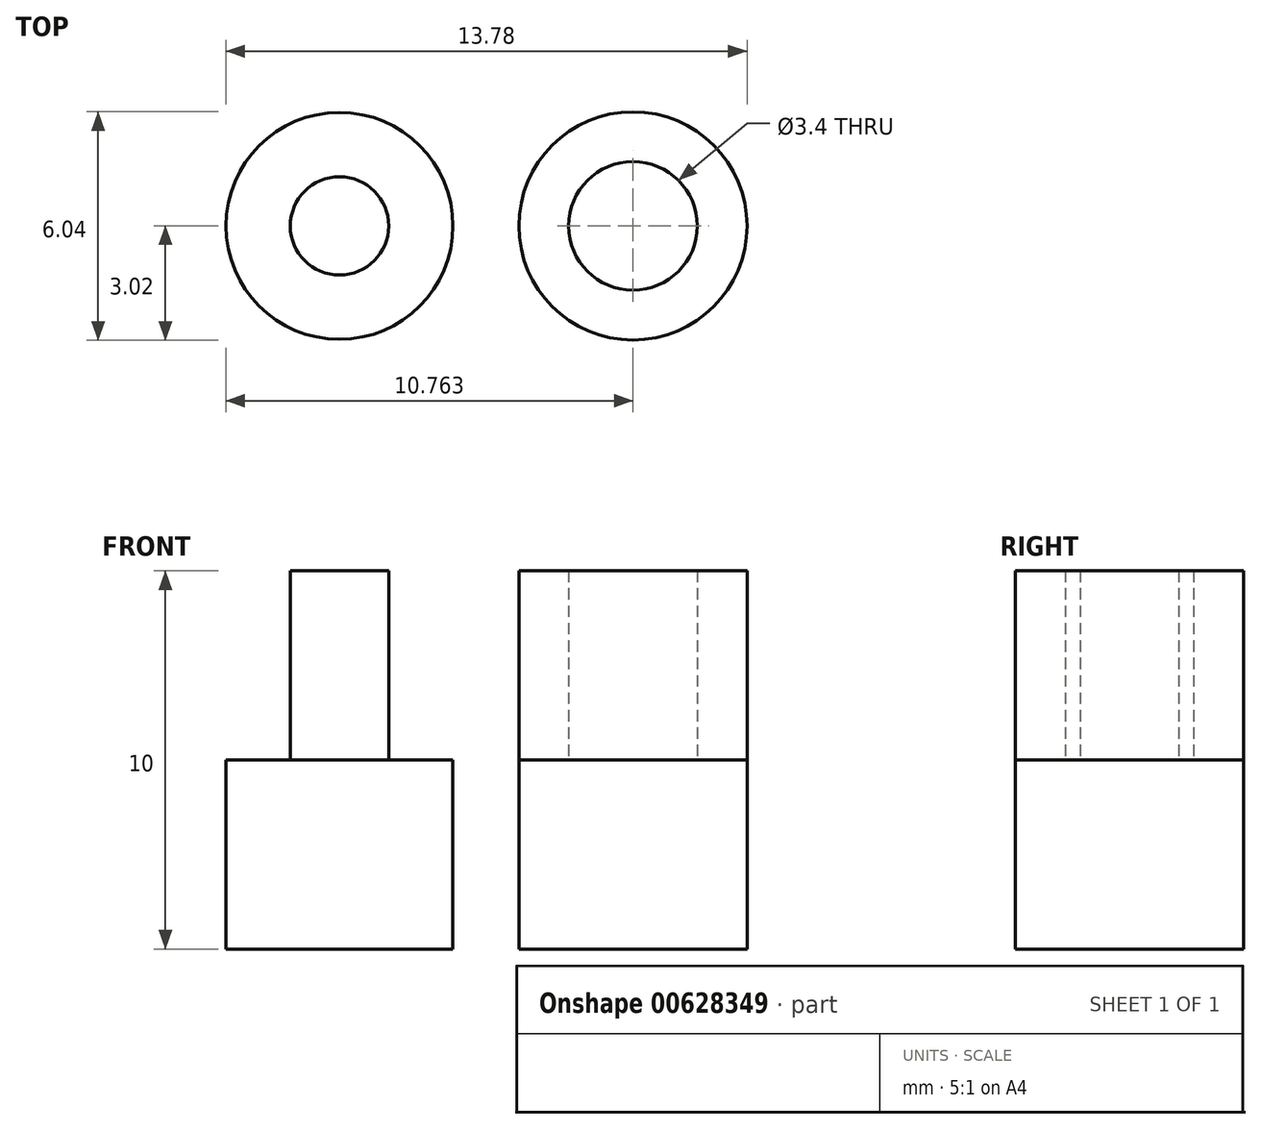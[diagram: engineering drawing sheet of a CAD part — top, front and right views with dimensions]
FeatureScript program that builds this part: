
annotation { "Feature Type Name" : "Feature", "Feature Type Description" : "" }
export const myFeature = defineFeature(function(context is Context, id is Id, definition is map)
    precondition{}
    {
        {
            var Q0;
            Q0=qCreatedBy(makeId("Top.planeOp"),FACE);
            var sketch = newSketch(context, id + "F0", { "sketchPlane" : qUnion([Q0])});
            skCircle(sketch, "E0", {"center": v(-33.58, 0) * mm, "radius": 3 * mm});
            skCircle(sketch, "E1", {"center": v(-25.82, 0) * mm, "radius": 3.02 * mm});
            skCircle(sketch, "E2", {"center": v(-33.58, 0) * mm, "radius": 1.3 * mm});
            skCircle(sketch, "E3", {"center": v(-25.82, 0) * mm, "radius": 1.7 * mm});
            skSolve(sketch);
        }
        {
            var Q0;
            Q0=makeQuery(id+"F0.imprint","IMPRINT",FACE,{"disambiguationData":[TD([[makeQuery(id+"F0.imprint","IMPRINT",EDGE,{"derivedFrom":sQuery(id+"F0.wireOp",EDGE,"E2")}),1.0]])]});
            var Q1;
            Q1=makeQuery(id+"F0.imprint","IMPRINT",FACE,{"disambiguationData":[TD([[makeQuery(id+"F0.imprint","IMPRINT",EDGE,{"derivedFrom":sQuery(id+"F0.wireOp",EDGE,"E0")}),1.0]])]});
            var Q2;
            Q2=makeQuery(id+"F0.imprint","IMPRINT",FACE,{"disambiguationData":[TD([[makeQuery(id+"F0.imprint","IMPRINT",EDGE,{"derivedFrom":sQuery(id+"F0.wireOp",EDGE,"E3")}),1.0]])]});
            var Q3;
            Q3=makeQuery(id+"F0.imprint","IMPRINT",FACE,{"disambiguationData":[TD([[makeQuery(id+"F0.imprint","IMPRINT",EDGE,{"derivedFrom":sQuery(id+"F0.wireOp",EDGE,"E1")}),1.0]])]});
            extrude(context, id + "F1", {"entities" : qUnion([Q0, Q1, Q2, Q3]), "oppositeDirection" : true, "depth" : 5 * mm, "offsetDistance" : 25 * mm});
        }
        {
            var Q0;
            Q0=makeQuery(id+"F0.imprint","IMPRINT",FACE,{"disambiguationData":[TD([[makeQuery(id+"F0.imprint","IMPRINT",EDGE,{"derivedFrom":sQuery(id+"F0.wireOp",EDGE,"E1")}),1.0]])]});
            var Q1;
            Q1=makeQuery(id+"F0.imprint","IMPRINT",FACE,{"disambiguationData":[TD([[makeQuery(id+"F0.imprint","IMPRINT",EDGE,{"derivedFrom":sQuery(id+"F0.wireOp",EDGE,"E2")}),1.0]])]});
            extrude(context, id + "F2", {"entities" : qUnion([Q0, Q1]), "depth" : 5 * mm, "offsetDistance" : 25 * mm});
        }
    });
